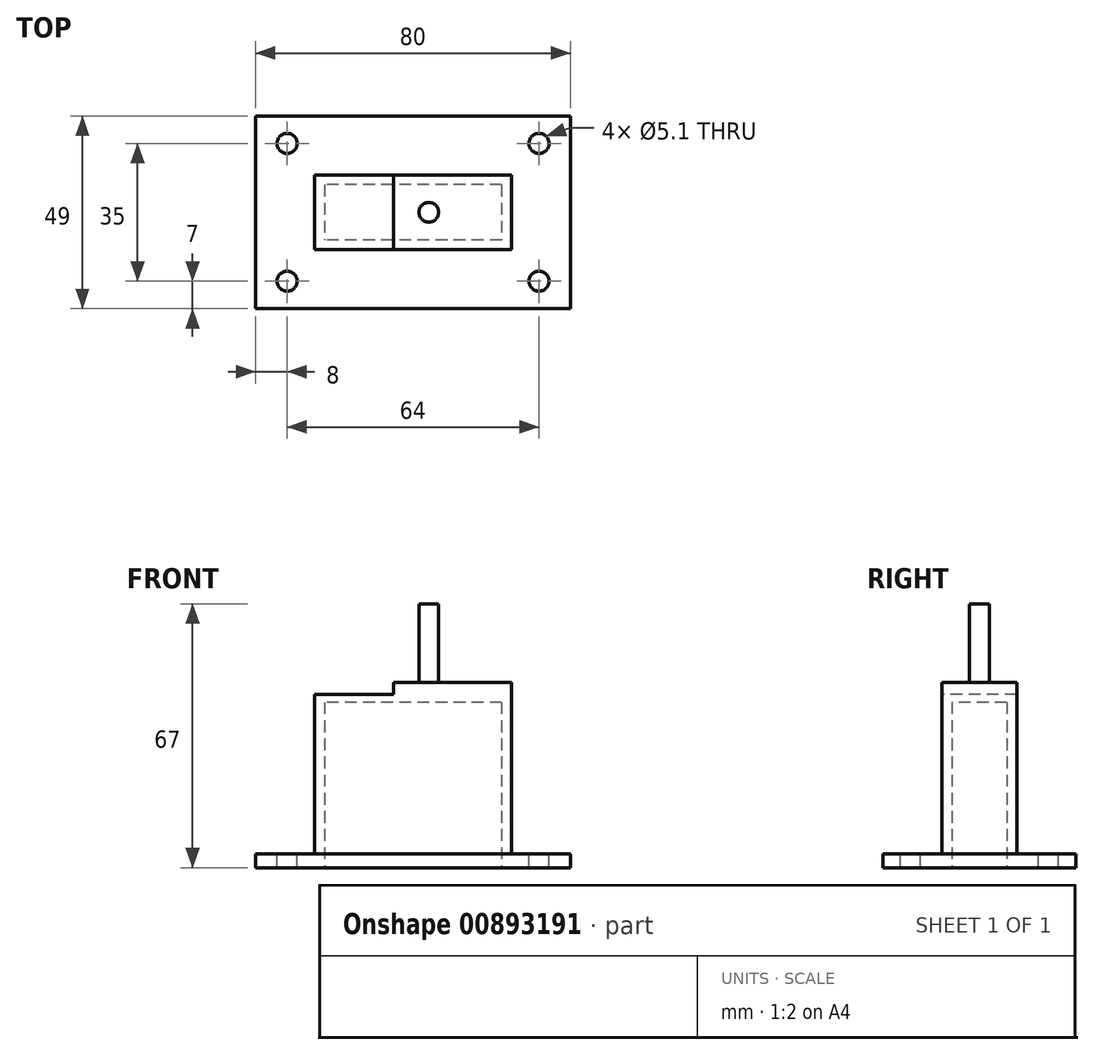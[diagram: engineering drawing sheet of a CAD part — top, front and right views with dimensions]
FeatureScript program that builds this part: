
annotation { "Feature Type Name" : "Feature", "Feature Type Description" : "" }
export const myFeature = defineFeature(function(context is Context, id is Id, definition is map)
    precondition{}
    {
        {
            var Q0;
            Q0=qCreatedBy(makeId("Top.planeOp"),FACE);
            var sketch = newSketch(context, id + "F0", { "sketchPlane" : qUnion([Q0])});
            skLineSegment(sketch, "E0.bottom", {"start": v(25, 9.5) * mm, "end": v(-25, 9.5) * mm});
            skLineSegment(sketch, "E0.top", {"start": v(25, -9.5) * mm, "end": v(-25, -9.5) * mm});
            skLineSegment(sketch, "E0.left", {"start": v(25, 9.5) * mm, "end": v(25, -9.5) * mm});
            skLineSegment(sketch, "E0.right", {"start": v(-25, 9.5) * mm, "end": v(-25, -9.5) * mm});
            skPoint(sketch, "E0.middle", {"position": v(0, 0) * mm});
            skSolve(sketch);
        }
        {
            var Q0;
            Q0 = qSketchRegion(id + "F0", true);
            extrude(context, id + "F1", {"entities" : qUnion([Q0]), "depth" : 44 * mm, "offsetDistance" : 25 * mm});
        }
        {
            var Q0;
            Q0=makeQuery(id+"F1.opExtrude","CAP_FACE",FACE,{"disambiguationData":[OSD([sQuery(id+"F0.wireOp",EDGE,"E0.bottom"),sQuery(id+"F0.wireOp",EDGE,"E0.top"),sQuery(id+"F0.wireOp",EDGE,"E0.left"),sQuery(id+"F0.wireOp",EDGE,"E0.right")])],"isStart":false});
            var sketch = newSketch(context, id + "F2", { "sketchPlane" : qUnion([Q0])});
            skLineSegment(sketch, "E1.bottom", {"start": v(25, 9.5) * mm, "end": v(-5, 9.5) * mm});
            skLineSegment(sketch, "E1.top", {"start": v(25, -9.5) * mm, "end": v(-5, -9.5) * mm});
            skLineSegment(sketch, "E1.left", {"start": v(25, 9.5) * mm, "end": v(25, -9.5) * mm});
            skLineSegment(sketch, "E1.right", {"start": v(-5, 9.5) * mm, "end": v(-5, -9.5) * mm});
            skSolve(sketch);
        }
        {
            var Q0;
            Q0 = qSketchRegion(id + "F2", true);
            extrude(context, id + "F3", {"entities" : qUnion([Q0]), "operationType" : NewBodyOperationType.ADD, "depth" : 3 * mm, "offsetDistance" : 25 * mm});
        }
        {
            var Q0;
            Q0=makeQuery(id+"F3.opExtrude","CAP_FACE",FACE,{"disambiguationData":[OSD([sQuery(id+"F2.wireOp",EDGE,"E1.bottom"),sQuery(id+"F2.wireOp",EDGE,"E1.top"),sQuery(id+"F2.wireOp",EDGE,"E1.left"),sQuery(id+"F2.wireOp",EDGE,"E1.right")])],"isStart":false});
            var sketch = newSketch(context, id + "F4", { "sketchPlane" : qUnion([Q0])});
            skCircle(sketch, "E2", {"center": v(4, 0) * mm, "radius": 2.5 * mm});
            skSolve(sketch);
        }
        {
            var Q0;
            Q0 = qSketchRegion(id + "F4", true);
            extrude(context, id + "F5", {"entities" : qUnion([Q0]), "operationType" : NewBodyOperationType.ADD, "depth" : 20 * mm, "offsetDistance" : 25 * mm});
        }
        {
            var Q0;
            Q0=makeQuery(id+"F1.opExtrude","CAP_FACE",FACE,{"disambiguationData":[OSD([sQuery(id+"F0.wireOp",EDGE,"E0.bottom"),sQuery(id+"F0.wireOp",EDGE,"E0.top"),sQuery(id+"F0.wireOp",EDGE,"E0.left"),sQuery(id+"F0.wireOp",EDGE,"E0.right")])],"isStart":true});
            var sketch = newSketch(context, id + "F6", { "sketchPlane" : qUnion([Q0])});
            skLineSegment(sketch, "E3.bottom", {"start": v(40, 24.5) * mm, "end": v(-40, 24.5) * mm});
            skLineSegment(sketch, "E3.top", {"start": v(40, -24.5) * mm, "end": v(-40, -24.5) * mm});
            skLineSegment(sketch, "E3.left", {"start": v(40, 24.5) * mm, "end": v(40, -24.5) * mm});
            skLineSegment(sketch, "E3.right", {"start": v(-40, 24.5) * mm, "end": v(-40, -24.5) * mm});
            skPoint(sketch, "E3.middle", {"position": v(0, 0) * mm});
            skSolve(sketch);
        }
        {
            var Q0;
            Q0 = qSketchRegion(id + "F6", true);
            extrude(context, id + "F7", {"entities" : qUnion([Q0]), "operationType" : NewBodyOperationType.ADD, "oppositeDirection" : true, "depth" : 3.5 * mm, "offsetDistance" : 25 * mm});
        }
        {
            var Q0;
            Q0=makeQuery(id+"F7.opExtrude","CAP_FACE",FACE,{"disambiguationData":[OSD([sQuery(id+"F6.wireOp",EDGE,"E3.bottom"),sQuery(id+"F6.wireOp",EDGE,"E3.top"),sQuery(id+"F6.wireOp",EDGE,"E3.left"),sQuery(id+"F6.wireOp",EDGE,"E3.right")])],"isStart":false});
            var sketch = newSketch(context, id + "F8", { "sketchPlane" : qUnion([Q0])});
            skCircle(sketch, "E4", {"center": v(-32, 17.5) * mm, "radius": 2.55 * mm});
            skCircle(sketch, "E5.MirrorC", {"center": v(32, 17.5) * mm, "radius": 2.55 * mm});
            skCircle(sketch, "E6.MirrorC", {"center": v(-32, -17.5) * mm, "radius": 2.55 * mm});
            skCircle(sketch, "E7.MirrorC", {"center": v(32, -17.5) * mm, "radius": 2.55 * mm});
            skSolve(sketch);
        }
        {
            var Q0;
            Q0 = qSketchRegion(id + "F8", true);
            extrude(context, id + "F9", {"entities" : qUnion([Q0]), "operationType" : NewBodyOperationType.REMOVE, "endBound" : BoundingType.UP_TO_NEXT, "oppositeDirection" : true, "depth" : 25 * mm, "offsetDistance" : 25 * mm});
        }
        {
            var Q0;
            Q0=makeQuery(id+"F7.boolean.opBoolean","MERGE",FACE,{"derivedFrom":[makeQuery(id+"F1.opExtrude","CAP_FACE",FACE,{"disambiguationData":[OSD([sQuery(id+"F0.wireOp",EDGE,"E0.bottom"),sQuery(id+"F0.wireOp",EDGE,"E0.top"),sQuery(id+"F0.wireOp",EDGE,"E0.left"),sQuery(id+"F0.wireOp",EDGE,"E0.right")])],"isStart":true}),makeQuery(id+"F7.opExtrude","CAP_FACE",FACE,{"disambiguationData":[OSD([sQuery(id+"F6.wireOp",EDGE,"E3.bottom"),sQuery(id+"F6.wireOp",EDGE,"E3.top"),sQuery(id+"F6.wireOp",EDGE,"E3.left"),sQuery(id+"F6.wireOp",EDGE,"E3.right")])],"isStart":true})]});
            var sketch = newSketch(context, id + "F10", { "sketchPlane" : qUnion([Q0])});
            skLineSegment(sketch, "E8.bottom", {"start": v(22.5, -7) * mm, "end": v(-22.5, -7) * mm});
            skLineSegment(sketch, "E8.top", {"start": v(22.5, 7) * mm, "end": v(-22.5, 7) * mm});
            skLineSegment(sketch, "E8.left", {"start": v(22.5, -7) * mm, "end": v(22.5, 7) * mm});
            skLineSegment(sketch, "E8.right", {"start": v(-22.5, -7) * mm, "end": v(-22.5, 7) * mm});
            skPoint(sketch, "E8.middle", {"position": v(0, 0) * mm});
            skSolve(sketch);
        }
        {
            var Q0;
            Q0 = qSketchRegion(id + "F10", true);
            extrude(context, id + "F11", {"entities" : qUnion([Q0]), "operationType" : NewBodyOperationType.REMOVE, "oppositeDirection" : true, "depth" : 42 * mm, "offsetDistance" : 25 * mm});
        }
    });
